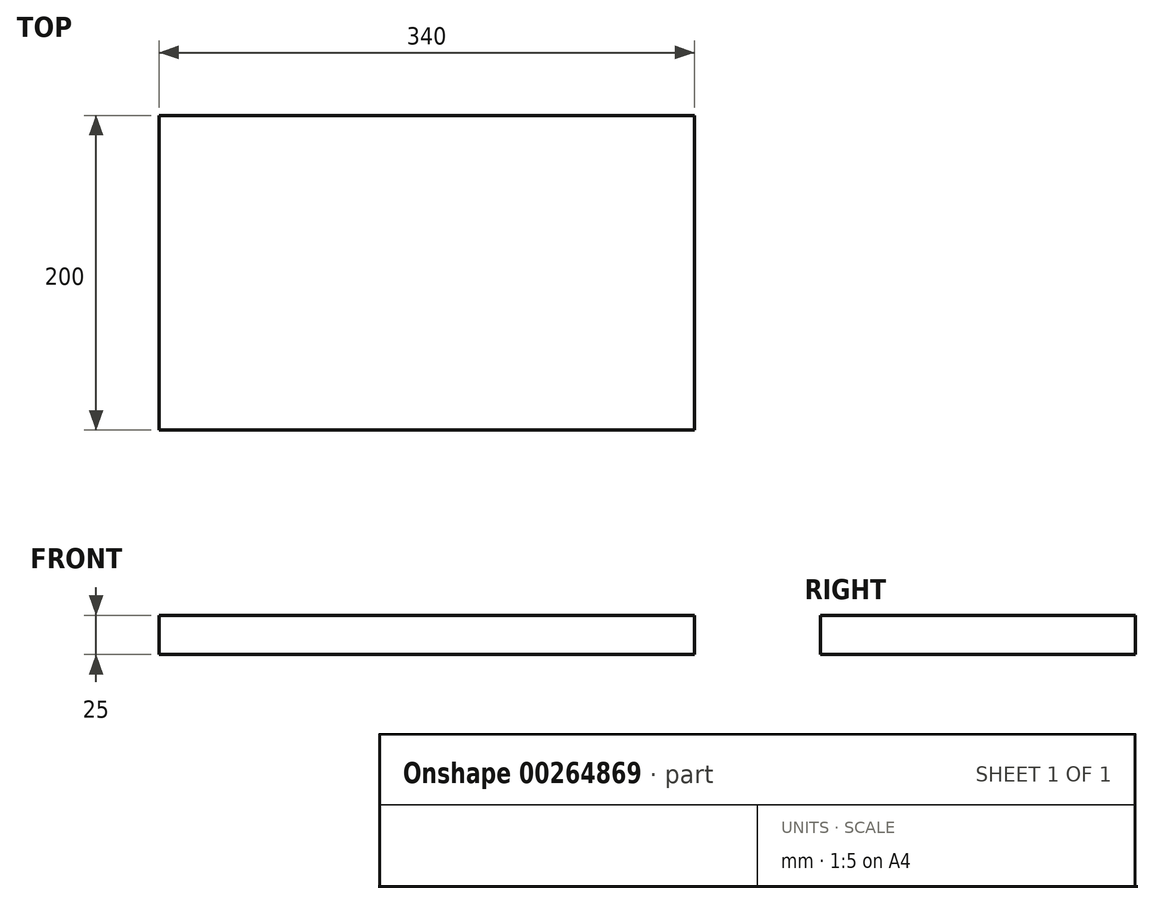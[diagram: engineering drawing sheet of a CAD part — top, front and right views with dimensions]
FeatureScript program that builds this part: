
annotation { "Feature Type Name" : "Feature", "Feature Type Description" : "" }
export const myFeature = defineFeature(function(context is Context, id is Id, definition is map)
    precondition{}
    {
        {
            var Q0;
            Q0=qCreatedBy(makeId("Top.planeOp"),FACE);
            var sketch = newSketch(context, id + "F0", { "sketchPlane" : qUnion([Q0])});
            skLineSegment(sketch, "E0.bottom", {"start": v(-170, 100) * mm, "end": v(170, 100) * mm});
            skLineSegment(sketch, "E0.top", {"start": v(-170, -100) * mm, "end": v(170, -100) * mm});
            skLineSegment(sketch, "E0.left", {"start": v(-170, 100) * mm, "end": v(-170, -100) * mm});
            skLineSegment(sketch, "E0.right", {"start": v(170, 100) * mm, "end": v(170, -100) * mm});
            skLineSegment(sketch, "E1", {"start": v(-170, 100) * mm, "end": v(170, -100) * mm, "construction": true});
            skPoint(sketch, "E2", {"position": v(0, 0) * mm});
            skSolve(sketch);
        }
        {
            var Q0;
            Q0=makeQuery(id+"F0.imprint","IMPRINT",FACE,{"disambiguationData":[TD([[makeQuery(id+"F0.imprint","IMPRINT",EDGE,{"derivedFrom":sQuery(id+"F0.wireOp",EDGE,"E0.bottom")}),-1.0]])]});
            extrude(context, id + "F1", {"entities" : qUnion([Q0]), "oppositeDirection" : true, "depth" : 25 * mm});
        }
    });
